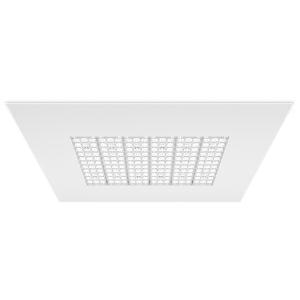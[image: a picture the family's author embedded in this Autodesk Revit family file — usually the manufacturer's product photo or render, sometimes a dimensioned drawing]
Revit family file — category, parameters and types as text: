
# Revit family: 3f_filippi_-_3f_six_r_ampio_3f_filippi_-_22233_-_3f_six_r_85-840_dali_wide_596x596
name_source: partatom
category: Lighting Fixtures
units: mm (PartAtom-declared; Revit-internal decimal feet)

## family parameters
Cut with Voids When Loaded = No
Host = Face
Light Source = No
Part Type = Normal
Room Calculation Point = No
Round Connector Dimension = Use Diameter
Shared = No

## types (1)
- 3F Filippi - 3F Six R Ampio (1 x LED, 13622 lm, 83 W, 4000 K)
    Apparent Load = 83 VA
    Approval mark = ENEC
    CIE Flux Codes = 61 95 99 100 100
    Color Rendering = 80
    Color Temperature = 4000 K
    Control Gear = Electronic transformer
    Default Elevation = 1800 mm
    Description = ILLUMINOTECHNICAL
Luminous efficiency 100% (DLOR 100%, ULOR 0%).
Initial luminous flux of the luminaire 13622 lm.
Direct symmetric distribution.
Installation Interdistance Transv.D = 1.39 x hu - Long.D = 1.43 x hu.
Tabular UGR (CIE 117 - 4H-8H; S=0.25H; 70/50/20): RUG 24.1 - 24.4.
Beam angle: 102° - 103°.
Luminous efficacy 164 lm/W.
Lifetime (L93/B10): 30000 h. (tq+25°C)
Lifetime (L90/B10): 50000 h. (tq+25°C)
Lifetime (L85/B10): 80000 h. (tq+25°C)
Lifetime (L80/B10): 100000 h. (tq+25°C)
Lifetime (L85/B10): 50000 h. (tq+35°C)
Sudden decreased luminous flux after 50000 hours: 0% (C0).
Photobiological safety in compliance with IEC/TR 62778: RG0 risk exempt, (IEC 62471).
In compliance with IEC/EN 62722-2-1 - IEC/EN 62717 standards.

SOURCE
Linear LED module 85W/840.
Energy efficiency class (UE 2019/2020 - UE 2019/2015): C.
CIE 13.3 Colour rendering index: CRI >80 (R9 <50%).
IES TM-30 Fidelity Index: Rf = 84 Rg = 95.
CCT nominal colour temperature 4000 K.
Colour initial tolerance (MacAdam): SDCM 3.

MECHANICAL
Housing in galvannealed steel, painted in white epoxy-polyester.
Methacrylate (PMMA) lenses with external flat surface.
Luminaire with limited surface temperature. - D - (EN 60598-2-24)
Dimensions: 596x596 mm, height 70 mm. Weight 4.94 kg.
IP40 protection degree.
Mechanical strength to impacts IK06 (1 joule).
Glow-wire test resistance 650°C.

ELECTRICAL
Halogen Free DALI-2, PUSH-DIM, electronic wiring 230V-50/60Hz, power factor 0.97 at full load, THD <25%, constant output current, class I, 1 driver, 1 DALI addresse.
Power of the luminaire 83 W.
CE - IEC 60598-1 - EN 60598-1.
SAFE FLICKER: PstLM=<1 and SVM=<0.4 (IEC TR 61547-1 and IEC TR 63158), to ensure a more comfortable and safe light.
Luminaire compliant with EN 60598-2-22 for power supply from a centralised emergency system CPSS (Central Power Supply System), not incorporated in the luminaire - high risk areas excluded. The default power and flux are 100% in AC and 15% in DC.
Ambient temperature from 0°C to +35°C.
Temperature class T6 max 85°C.
Power cable type H05Z1Z1-F 5x1.5 mm² that protrudes by 1 m with sheared ends.
Relative humidity UR: <85%.

INSTALLATION
Lay-in recessed fitting.
All accessories dedicated to this product are available on the Catalog and on our website www.3F-Filippi.com.

APPLICATIONS
Suitable product for food production plants (HACCP), IFS (Food Version 6), BRC (GSFS Food Version 7).
Environments: commercial, exhibition areas, transit areas, lobbies or waiting rooms, shops.

LIGHT MANAGEMENT
Recommended minimum setting: 10%.
The device, equipped with DALI-2 driver, can be controlled manually with 3F Easy Dim technology or automatically/manually with 3F Smart Dimming technology and/or centralised DALI systems.
DALI-2 certification guarantees interoperability with other devices with the same certification.
In electrical systems without a regulation system (manual or automatic) and DALI bus, a suitable jumper must be made on the DA-DA terminals of the appliance.

WARNING
Luminaire designed for disposal/recycling at end-of-life.
Replaceable (LED only) light source by a professional. Replaceable control gear by a professional.
    Height = 0 mm  [stored 0 ft]
    Lamp = 1 x LED
    Lamp Light Flux = 13622 lm
    Lamp Power = 83 W
    Lamp count = 1
    Length = 596 mm
    Lifetime = 50000 h
    Luminous efficacy = 164 lm/W
    Manufacturer = 3F Filippi
    ModVariant = No
    Model = 3F Filippi - 22233 - 3F Six R 85-840 DALI WIDE 596x596
    Mounting Place = Ceiling
    Mounting Type = Recessed
    Number of Poles = 1
    OnlyDefault = Yes
    Power Factor = 1
    Product Name = 3F Filippi - 3F Six R Ampio
    Product group = recessed luminaire
    ProductGroupID = 4
    Protection Class = Protection class I
    Protection Degree = IP 40
    RLX_Detail_Level = 1
    RLX_Emergency_Light_Flux = 0 lm
    RLX_Emergency_Type = 0
    RLX_Emergency_Type_DB = No
    RlxData = <blob elided: 129121 chars, md5=78a8c0b8>
    Socket = socket
    Standby Power = 0 W
    System Light Flux = 13622 lm
    System Power = 83 W
    Type Comments = Product without accessories
    Type Image = 3ffilippi_3f_six_r_ampio.jpg
    URL = http://relux.com
    VarID = ---
    Voltage = 0 V
    Weight = 0.00 kg
    Width = 596 mm

note: [stored X ft] marks values corroborated as IEEE doubles in the binary element streams (Revit-internal decimal feet)

## geometry (parser evidence)
native form markers: Blend x4, Sweep x9
no freeform markers — native parametric forms only
